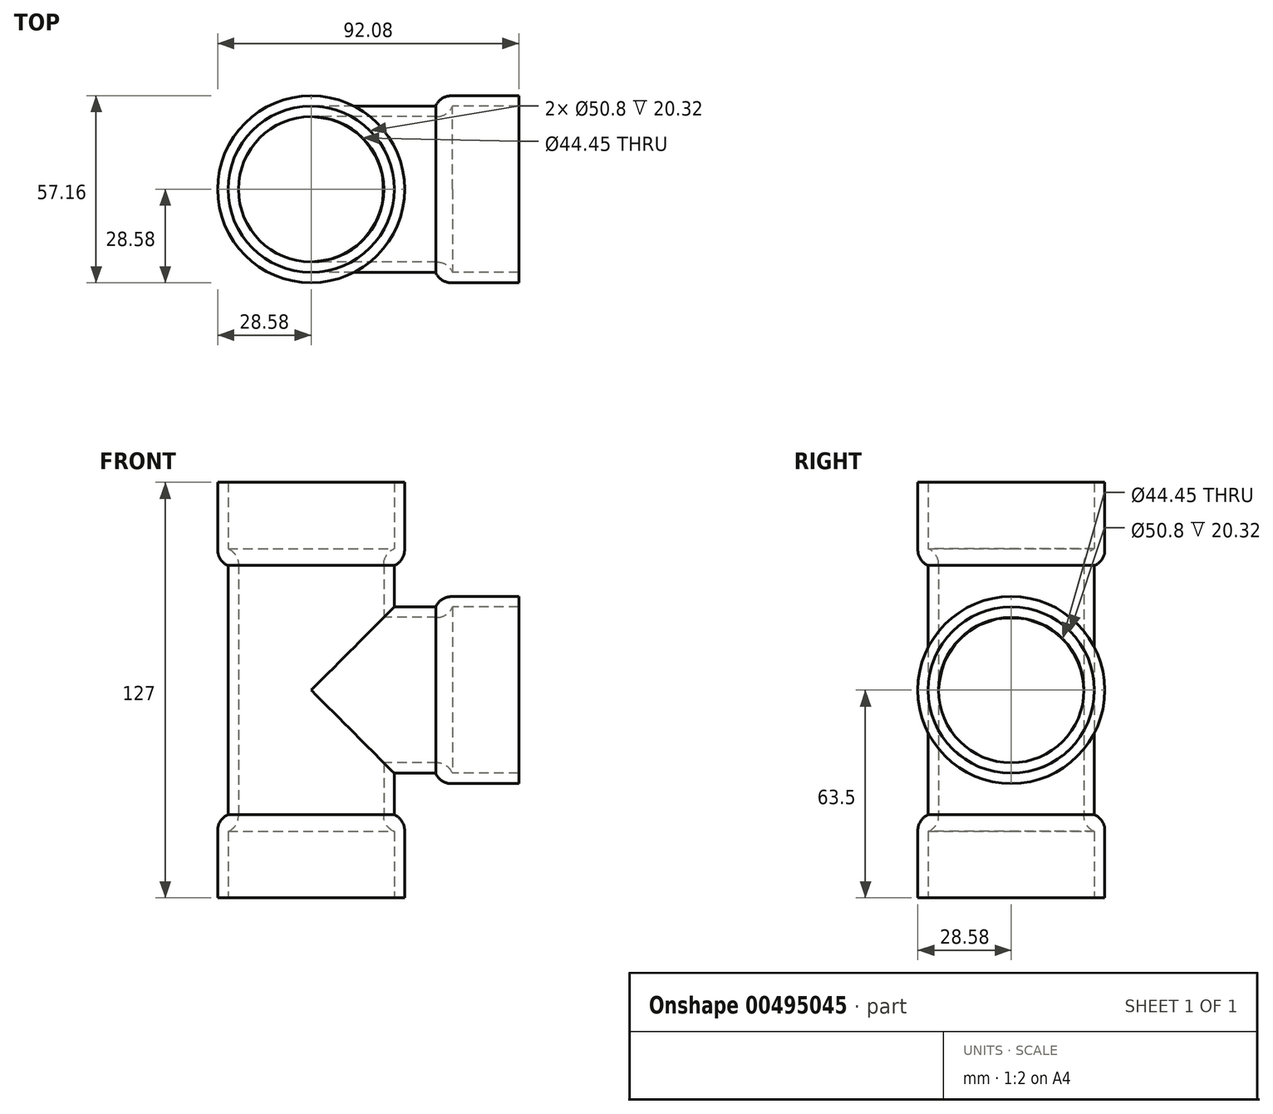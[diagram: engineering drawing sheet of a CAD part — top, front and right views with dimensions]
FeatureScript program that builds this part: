
annotation { "Feature Type Name" : "Feature", "Feature Type Description" : "" }
export const myFeature = defineFeature(function(context is Context, id is Id, definition is map)
    precondition{}
    {
        {
            var Q0;
            Q0=qCreatedBy(makeId("Front.planeOp"),FACE);
            var sketch = newSketch(context, id + "F0", { "sketchPlane" : qUnion([Q0])});
            skLineSegment(sketch, "E0", {"start": v(0, 38.1) * mm, "end": v(0, -38.1) * mm});
            skLineSegment(sketch, "E1", {"start": v(0, -38.1) * mm, "end": v(-3.17, -38.1) * mm});
            skLineSegment(sketch, "E2", {"start": v(-3.17, -38.1) * mm, "end": v(-3.17, -63.5) * mm});
            skLineSegment(sketch, "E3", {"start": v(-3.17, -63.5) * mm, "end": v(0, -63.5) * mm});
            skLineSegment(sketch, "E4", {"start": v(0, -63.5) * mm, "end": v(0, -43.18) * mm});
            skLineSegment(sketch, "E5", {"start": v(0, -43.18) * mm, "end": v(3.17, -43.18) * mm});
            skLineSegment(sketch, "E6", {"start": v(3.18, -43.18) * mm, "end": v(3.18, 43.18) * mm});
            skLineSegment(sketch, "E7", {"start": v(3.17, 43.18) * mm, "end": v(0, 43.18) * mm});
            skLineSegment(sketch, "E8", {"start": v(0, 43.18) * mm, "end": v(0, 63.5) * mm});
            skLineSegment(sketch, "E9", {"start": v(0, 63.5) * mm, "end": v(-3.18, 63.5) * mm});
            skLineSegment(sketch, "E10", {"start": v(-3.18, 63.5) * mm, "end": v(-3.17, 38.1) * mm});
            skLineSegment(sketch, "E11", {"start": v(-3.17, 38.1) * mm, "end": v(0, 38.1) * mm});
            skLineSegment(sketch, "E12", {"start": v(0, 0) * mm, "end": v(50.8, 0) * mm});
            skLineSegment(sketch, "E13", {"start": v(25.4, 0) * mm, "end": v(25.4, -96.62) * mm});
            skLineSegment(sketch, "E14", {"start": v(25.4, 0) * mm, "end": v(25.4, 86.15) * mm});
            skLineSegment(sketch, "E15", {"start": v(50.8, 0) * mm, "end": v(50.8, -25.4) * mm});
            skLineSegment(sketch, "E16", {"start": v(50.8, -25.4) * mm, "end": v(63.5, -25.4) * mm});
            skLineSegment(sketch, "E17", {"start": v(63.5, -25.4) * mm, "end": v(63.5, -28.57) * mm});
            skLineSegment(sketch, "E18", {"start": v(63.5, -28.58) * mm, "end": v(88.9, -28.58) * mm});
            skLineSegment(sketch, "E19", {"start": v(88.9, -28.57) * mm, "end": v(88.9, -25.4) * mm});
            skLineSegment(sketch, "E20", {"start": v(88.9, -25.4) * mm, "end": v(68.58, -25.4) * mm});
            skLineSegment(sketch, "E21", {"start": v(68.58, -25.4) * mm, "end": v(68.58, -22.23) * mm});
            skLineSegment(sketch, "E22", {"start": v(68.58, -22.23) * mm, "end": v(50.8, -22.23) * mm});
            skLineSegment(sketch, "E23", {"start": v(50.8, -22.23) * mm, "end": v(25.4, -22.23) * mm});
            skLineSegment(sketch, "E24", {"start": v(50.8, -25.4) * mm, "end": v(25.4, -25.4) * mm});
            skLineSegment(sketch, "E25", {"start": v(50.8, 0) * mm, "end": v(136.16, 0) * mm});
            skSolve(sketch);
        }
        {
            var Q0;
            {var subQ0=sQuery(id+"F0.wireOp",EDGE,"E7");Q0=makeQuery(id+"F0.imprint","IMPRINT",FACE,{"disambiguationData":[TD([[makeQuery(id+"F0.imprint","IMPRINT",EDGE,{"derivedFrom":subQ0}),1.0]])]});}
            var Q1;
            {var subQ5=sQuery(id+"F0.wireOp",EDGE,"E1");Q1=makeQuery(id+"F0.imprint","IMPRINT",FACE,{"disambiguationData":[TD([[makeQuery(id+"F0.imprint","IMPRINT",EDGE,{"derivedFrom":subQ5}),1.0]])]});}
            var Q2;
            Q2=sQuery(id+"F0.wireOp",EDGE,"E14");
            revolve(context, id + "F1", {"entities" : qUnion([Q0, Q1]), "axis" : qUnion([Q2]), "revolveType" : RevolveType.FULL});
        }
        {
            var Q0;
            {var subQ0=sQuery(id+"F0.wireOp",EDGE,"E16");Q0=makeQuery(id+"F0.imprint","IMPRINT",FACE,{"disambiguationData":[TD([[makeQuery(id+"F0.imprint","IMPRINT",EDGE,{"derivedFrom":subQ0}),1.0]])]});}
            var Q1;
            {var subQ0=sQuery(id+"F0.wireOp",EDGE,"E23");Q1=makeQuery(id+"F0.imprint","IMPRINT",FACE,{"disambiguationData":[TD([[makeQuery(id+"F0.imprint","IMPRINT",EDGE,{"derivedFrom":subQ0}),1.0]])]});}
            var Q2;
            Q2=sQuery(id+"F0.wireOp",EDGE,"E12");
            revolve(context, id + "F2", {"operationType" : NewBodyOperationType.ADD, "entities" : qUnion([Q0, Q1]), "axis" : qUnion([Q2]), "revolveType" : RevolveType.FULL});
        }
        {
            var Q0;
            Q0=makeQuery(id+"F1.opRevolve","SWEPT_EDGE",EDGE,{"disambiguationData":[OSD([sQuery(id+"F0.wireOp",EDGE,"E10"),sQuery(id+"F0.wireOp",EDGE,"E11")])]});
            var Q1;
            Q1=makeQuery(id+"F1.opRevolve","SWEPT_EDGE",EDGE,{"disambiguationData":[OSD([sQuery(id+"F0.wireOp",EDGE,"E1"),sQuery(id+"F0.wireOp",EDGE,"E2")])]});
            var Q2;
            Q2=makeQuery(id+"F2.opRevolve","SWEPT_EDGE",EDGE,{"disambiguationData":[OSD([sQuery(id+"F0.wireOp",EDGE,"E17"),sQuery(id+"F0.wireOp",EDGE,"E18")])]});
            var Q3;
            Q3=makeQuery(id+"F2.opRevolve","SWEPT_EDGE",EDGE,{"disambiguationData":[OSD([sQuery(id+"F0.wireOp",EDGE,"E21"),sQuery(id+"F0.wireOp",EDGE,"E22")])]});
            var Q4;
            Q4=makeQuery(id+"F1.opRevolve","SWEPT_EDGE",EDGE,{"disambiguationData":[OSD([sQuery(id+"F0.wireOp",EDGE,"E6"),sQuery(id+"F0.wireOp",EDGE,"E7")])]});
            var Q5;
            Q5=makeQuery(id+"F1.opRevolve","SWEPT_EDGE",EDGE,{"disambiguationData":[OSD([sQuery(id+"F0.wireOp",EDGE,"E5"),sQuery(id+"F0.wireOp",EDGE,"E6")])]});
            fillet(context, id + "F3", {"entities" : qUnion([Q0, Q1, Q2, Q3, Q4, Q5]), "radius" : 5.08 * mm, "tangentPropagation" : true, "allowEdgeOverflow" : false});
        }
        {
            var Q0;
            Q0=makeQuery(id+"F2.opRevolve","SWEPT_FACE",FACE,{"disambiguationData":[OSD([sQuery(id+"F0.wireOp",EDGE,"E19")])]});
            var sketch = newSketch(context, id + "F4", { "sketchPlane" : qUnion([Q0])});
            skCircle(sketch, "E26.0", {"center": v(0, 0) * mm, "radius": 22.23 * mm});
            skSolve(sketch);
        }
        {
            var Q0;
            Q0=makeQuery(id+"F4.imprint","IMPRINT",FACE,{"disambiguationData":[TD([[makeQuery(id+"F4.imprint","IMPRINT",EDGE,{"derivedFrom":sQuery(id+"F4.wireOp",EDGE,"E26.0")}),1.0]])]});
            var Q1;
            Q1=makeQuery(id+"F2.boolean.opBoolean","SPLIT",FACE,{"disambiguationData":[OD(0.0)],"derivedFrom":makeQuery(id+"F2.opRevolve","SWEPT_FACE",FACE,{"disambiguationData":[OSD([sQuery(id+"F0.wireOp",EDGE,"E13")])]})});
            extrude(context, id + "F5", {"entities" : qUnion([Q0]), "operationType" : NewBodyOperationType.REMOVE, "endBound" : BoundingType.UP_TO_SURFACE, "oppositeDirection" : true, "endBoundEntityFace" : qUnion([Q1]), "depth" : 25.4 * mm});
        }
        {
            var Q0;
            Q0=makeQuery(id+"F1.opRevolve","SWEPT_FACE",FACE,{"disambiguationData":[OSD([sQuery(id+"F0.wireOp",EDGE,"E3")])]});
            var sketch = newSketch(context, id + "F6", { "sketchPlane" : qUnion([Q0])});
            skCircle(sketch, "E27.0", {"center": v(25.4, 0) * mm, "radius": 22.23 * mm});
            skSolve(sketch);
        }
        {
            var Q0;
            Q0=makeQuery(id+"F6.imprint","IMPRINT",FACE,{"disambiguationData":[TD([[makeQuery(id+"F6.imprint","IMPRINT",EDGE,{"derivedFrom":sQuery(id+"F6.wireOp",EDGE,"E27.0")}),1.0]])]});
            extrude(context, id + "F7", {"entities" : qUnion([Q0]), "operationType" : NewBodyOperationType.REMOVE, "endBound" : BoundingType.THROUGH_ALL, "oppositeDirection" : true, "depth" : 25.4 * mm});
        }
    });
